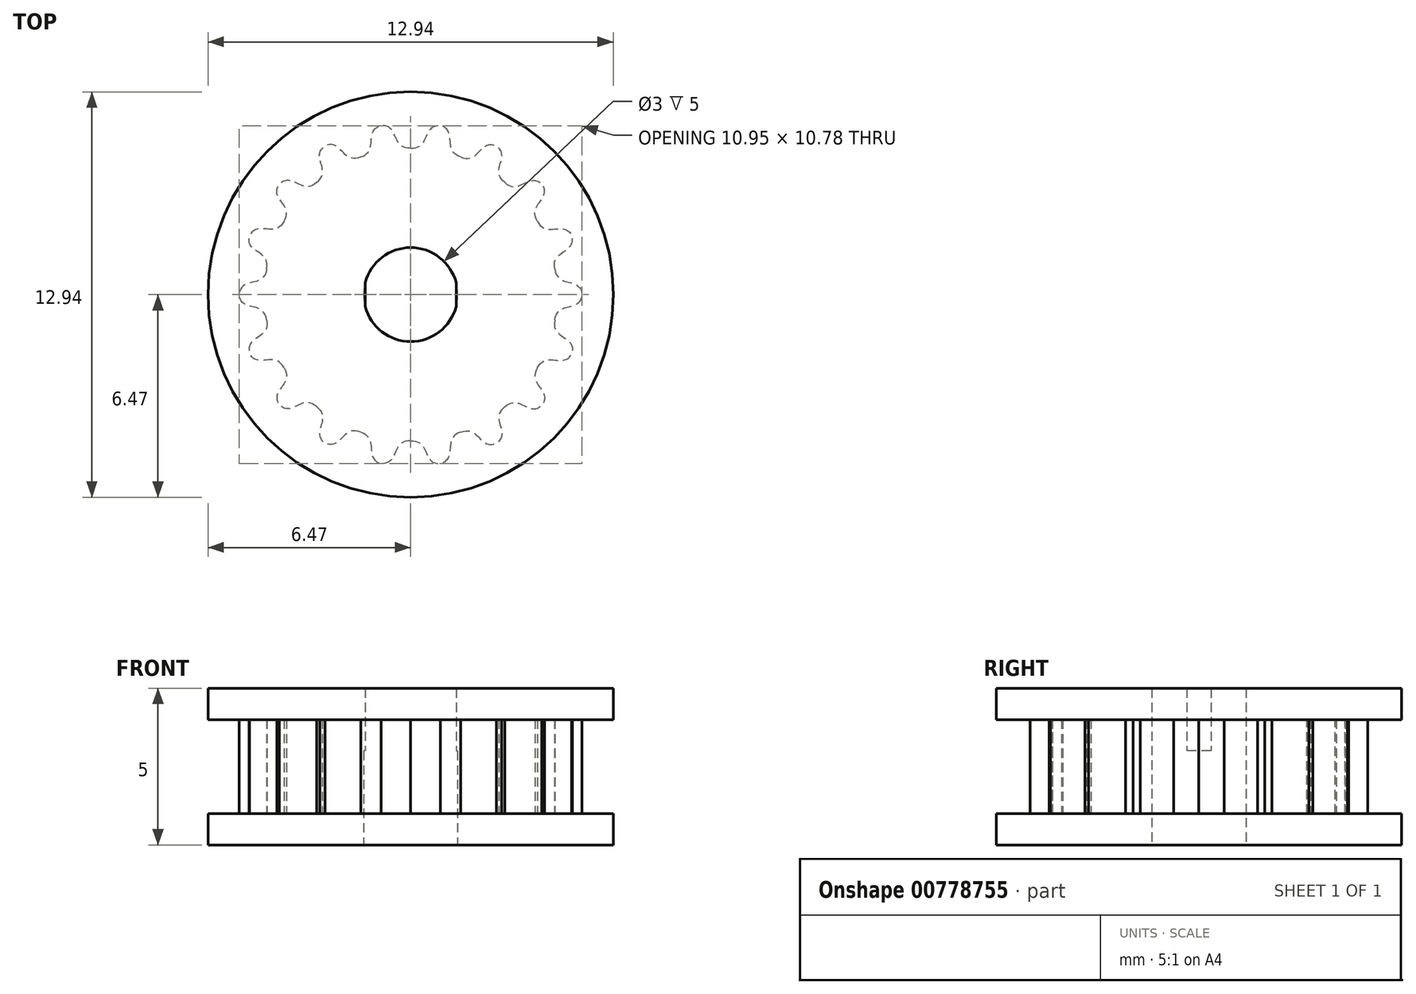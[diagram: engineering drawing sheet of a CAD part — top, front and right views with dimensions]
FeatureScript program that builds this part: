
annotation { "Feature Type Name" : "Feature", "Feature Type Description" : "" }
export const myFeature = defineFeature(function(context is Context, id is Id, definition is map)
    precondition{}
    {
        {
            assignVariable(context, id + "F0", {"name" : "teeth", "anyValue" : 18});
        }
        {
            var Q0;
            Q0=qCreatedBy(makeId("Top.planeOp"),FACE);
            var sketch = newSketch(context, id + "F1", { "sketchPlane" : qUnion([Q0])});
            skCircle(sketch, "E0", {"center": v(0, 0) * mm, "radius": 5.47 * mm, "construction": true});
            skLineSegment(sketch, "E1", {"start": v(0, 0) * mm, "end": v(0, 5.47) * mm, "construction": true});
            skLineSegment(sketch, "E2", {"start": v(0, 0) * mm, "end": v(0.95, 5.4) * mm, "construction": true});
            skArc(sketch, "E3", {"start": v(0.81, 4.6) * mm, "mid": v(0.4, 4.66) * mm, "end": v(0, 4.67) * mm, "construction": true});
            skLineSegment(sketch, "E4", {"start": v(0.61, 5.44) * mm, "end": v(0, 1.98) * mm, "construction": true});
            skFitSpline(sketch, "E5", {"points": [v(0, 4.67) * mm, v(0.57, 5.2) * mm, v(0.95, 5.4) * mm], "startDerivative": vector(2.16, -0.1) * mm, "endDerivative": vector(1.18, -0.19) * mm});
            skFitSpline(sketch, "E6.MirrorCS", {"points": [v(0, 4.67) * mm, v(-0.57, 5.2) * mm, v(-0.95, 5.4) * mm], "startDerivative": vector(-2.16, -0.1) * mm, "endDerivative": vector(-1.18, -0.19) * mm});
            skArc(sketch, "E7", {"start": v(0.95, 5.4) * mm, "mid": v(0, 5.47) * mm, "end": v(-0.95, 5.4) * mm});
            skLineSegment(sketch, "E8", {"start": v(-0.95, 5.4) * mm, "end": v(-1.12, 6.37) * mm});
            skArc(sketch, "E9", {"start": v(1.12, 6.37) * mm, "mid": v(0, 6.47) * mm, "end": v(-1.12, 6.37) * mm});
            skLineSegment(sketch, "E10", {"start": v(1.12, 6.37) * mm, "end": v(0.95, 5.4) * mm});
            skSolve(sketch);
        }
        {
            var Q0;
            Q0=qCreatedBy(makeId("Top.planeOp"),FACE);
            var sketch = newSketch(context, id + "F2", { "sketchPlane" : qUnion([Q0])});
            skCircle(sketch, "E11", {"center": v(0, 0) * mm, "radius": 6.47 * mm});
            skCircle(sketch, "E12", {"center": v(0, 0) * mm, "radius": 1.5 * mm});
            skLineSegment(sketch, "E13", {"start": v(-1.45, 0.38) * mm, "end": v(-1.45, -0.38) * mm});
            skLineSegment(sketch, "E14", {"start": v(1.45, 0.38) * mm, "end": v(1.45, -0.38) * mm});
            skSolve(sketch);
        }
        {
            var Q0;
            Q0=makeQuery(id+"F2.imprint","IMPRINT",FACE,{"disambiguationData":[TD([[makeQuery(id+"F2.imprint","IMPRINT",EDGE,{"derivedFrom":sQuery(id+"F2.wireOp",EDGE,"E11")}),1.0]])]});
            var Q1;
            {var subQ0=sQuery(id+"F2.wireOp",EDGE,"E13");Q1=makeQuery(id+"F2.imprint","IMPRINT",FACE,{"disambiguationData":[TD([[makeQuery(id+"F2.imprint","IMPRINT",EDGE,{"derivedFrom":subQ0}),-1.0]])]});}
            var Q2;
            {var subQ0=sQuery(id+"F2.wireOp",EDGE,"E14");Q2=makeQuery(id+"F2.imprint","IMPRINT",FACE,{"disambiguationData":[TD([[makeQuery(id+"F2.imprint","IMPRINT",EDGE,{"derivedFrom":subQ0}),1.0]])]});}
            extrude(context, id + "F3", {"entities" : qUnion([Q0, Q1, Q2]), "depth" : 2.5 * mm, "offsetDistance" : 25 * mm});
        }
        {
            var Q0;
            Q0=makeQuery(id+"F2.imprint","IMPRINT",FACE,{"disambiguationData":[TD([[makeQuery(id+"F2.imprint","IMPRINT",EDGE,{"derivedFrom":sQuery(id+"F2.wireOp",EDGE,"E11")}),1.0]])]});
            extrude(context, id + "F4", {"entities" : qUnion([Q0]), "operationType" : NewBodyOperationType.ADD, "oppositeDirection" : true, "depth" : 2.5 * mm, "offsetDistance" : 25 * mm});
        }
        {
            var Q0;
            Q0 = qSketchRegion(id + "F1", true);
            extrude(context, id + "F5", {"entities" : qUnion([Q0]), "endBound" : BoundingType.SYMMETRIC, "depth" : 3 * mm, "offsetDistance" : 25 * mm});
        }
        {
            var Q0;
            Q0=makeQuery(id+"F5.opExtrude","SWEPT_BODY",BODY,{"disambiguationData":[OSD([sQuery(id+"F1.wireOp",EDGE,"E5"),sQuery(id+"F1.wireOp",EDGE,"E6.MirrorCS"),sQuery(id+"F1.wireOp",EDGE,"E7")])]});
            var Q1;
            Q1=sQuery(id+"F1.wireOp",EDGE,"E0");
            circularPattern(context, id + "F6", {"operationType" : NewBodyOperationType.REMOVE, "entities" : qUnion([Q0]), "axis" : qUnion([Q1]), "angle" : 360 * degree, "instanceCount" : getVariable(context, 'teeth'), "equalSpace" : true});
        }
        {
            var Q0;
            Q0 = qSketchRegion(id + "F2", true);
            var Q1;
            {var subQ0=sQuery(id+"F2.wireOp",EDGE,"E14");Q1=makeQuery(id+"F2.imprint","IMPRINT",FACE,{"disambiguationData":[TD([[makeQuery(id+"F2.imprint","IMPRINT",EDGE,{"derivedFrom":subQ0}),1.0]])]});}
            var Q2;
            {var subQ0=sQuery(id+"F2.wireOp",EDGE,"E13");Q2=makeQuery(id+"F2.imprint","IMPRINT",FACE,{"disambiguationData":[TD([[makeQuery(id+"F2.imprint","IMPRINT",EDGE,{"derivedFrom":subQ0}),1.0]])]});}
            var Q3;
            {var subQ0=sQuery(id+"F2.wireOp",EDGE,"E13");Q3=makeQuery(id+"F2.imprint","IMPRINT",FACE,{"disambiguationData":[TD([[makeQuery(id+"F2.imprint","IMPRINT",EDGE,{"derivedFrom":subQ0}),-1.0]])]});}
            extrude(context, id + "F7", {"entities" : qUnion([Q0, Q1, Q2, Q3]), "operationType" : NewBodyOperationType.REMOVE, "endBound" : BoundingType.SYMMETRIC, "oppositeDirection" : true, "depth" : 1 * mm, "offsetDistance" : 25 * mm});
        }
        {
            var Q0;
            Q0=makeQuery(id+"F7.boolean.opBoolean","SPLIT",BODY,{"disambiguationData":[OD(0.0)],"derivedFrom":makeQuery(id+"F3.opExtrude","SWEPT_BODY",BODY,{"disambiguationData":[OSD([sQuery(id+"F2.wireOp",EDGE,"E11"),sQuery(id+"F2.wireOp",EDGE,"E12"),sQuery(id+"F2.wireOp",EDGE,"E13"),sQuery(id+"F2.wireOp",EDGE,"E14")])]})});
            transform(context, id + "F8", {"entities" : qUnion([Q0]), "transformType" : TransformType.TRANSLATION_3D, "dx" : 0 * mm, "dy" : 0 * mm, "dz" : -10 * mm, "makeCopy" : false});
        }
        {
            var Q0;
            Q0=makeQuery(id+"F7.boolean.opBoolean","COPY",FACE,{"derivedFrom":makeQuery(id+"F7.opExtrude","CAP_FACE",FACE,{"disambiguationData":[OSD([sQuery(id+"F2.wireOp",EDGE,"E11")])],"isStart":false})});
            extrude(context, id + "F9", {"entities" : qUnion([Q0]), "operationType" : NewBodyOperationType.ADD, "depth" : 3 * mm, "offsetDistance" : 25 * mm});
        }
    });
